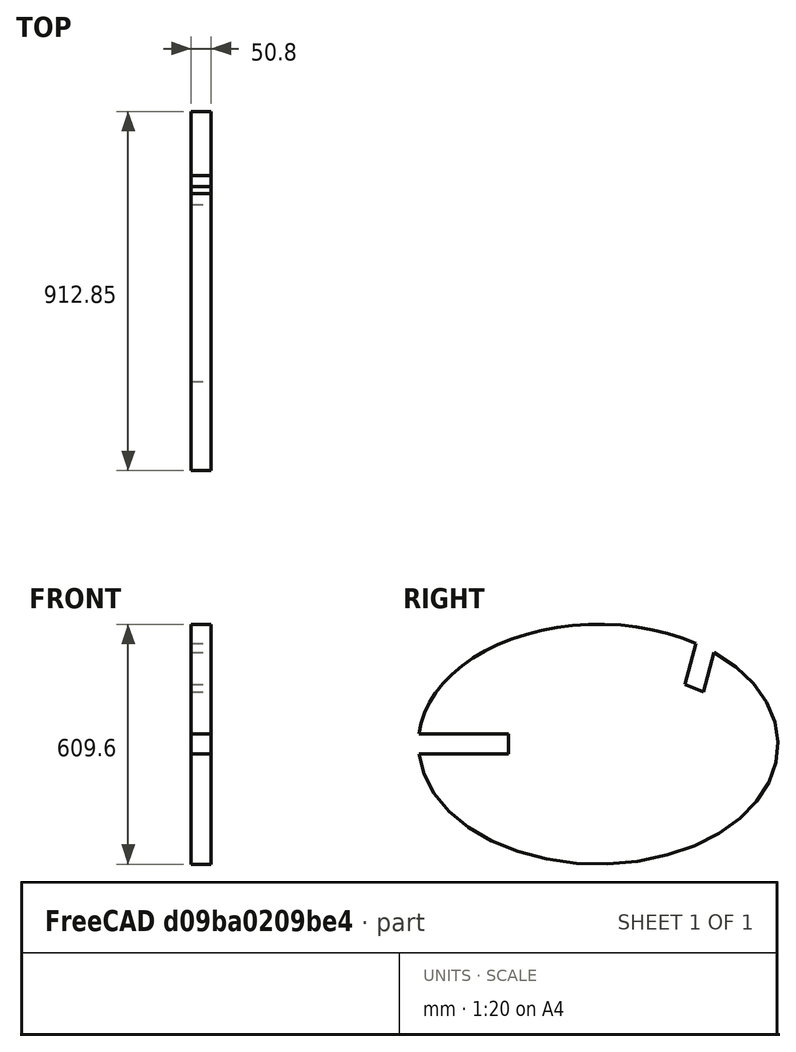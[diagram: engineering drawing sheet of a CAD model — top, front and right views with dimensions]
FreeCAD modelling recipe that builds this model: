
FCSTD DOCUMENT  (FreeCAD 0.21R33771 (Git))
Label: eclipse-2-side
License: All rights reserved
LicenseURL: http://en.wikipedia.org/wiki/All_rights_reserved
objects: Sketcher::SketchObject×1, PartDesign::Pad×1, PartDesign::Body×1, Spreadsheet::Sheet×1
note: 4 computed .brp shape members not serialized (recipe doc carries the construction recipe); baked Part::Feature solids carry a one-line shape summary decoded from their .brp

FEATURE [Sketcher::SketchObject] Sketch
  FullyConstrained = false
  MapMode = 5
  Placement = pos=(0,0,0) rot=(0.57735,0.57735,0.57735;2.0944rad)
  Support = -> [YZ_Plane]
  expr: Constraints[11] = <<dims>>.thickness
  expr: Constraints[18] = <<dims>>.thickness
  expr: Constraints[5] = <<dims>>.eclipse_height
  expr: Constraints[6] = <<dims>>.eclipse_length
  sketch-geometry (12):
    g0: ArcOfEllipse CenterX=0 CenterY=0 CenterZ=0 NormalX=0 NormalY=0 NormalZ=1 MajorRadius=457.2 MinorRadius=304.8 AngleXU=3.14063 StartAngle=0.082882 EndAngle=4.01486
    g1: LineSegment StartX=-457.2 StartY=0.438159 StartZ=0 EndX=457.2 EndY=-0.438159 EndZ=0
    g2: LineSegment StartX=-0.292106 StartY=-304.8 StartZ=0 EndX=0.292106 EndY=304.8 EndZ=0
    g3: GeomPoint X=-340.777 Y=0.326584 Z=0
    g4: GeomPoint X=340.777 Y=-0.326584 Z=0
    g5: LineSegment StartX=-455.564 StartY=26.0031 StartZ=0 EndX=-228.6 EndY=26.0031 EndZ=0
    g6: LineSegment StartX=-455.655 StartY=-24.7969 StartZ=0 EndX=-228.6 EndY=-24.7969 EndZ=0
    g7: LineSegment StartX=-228.6 StartY=-24.7969 StartZ=0 EndX=-228.6 EndY=26.0031 EndZ=0
    g8: LineSegment StartX=293.896 StartY=233.326 StartZ=0 EndX=266.795 EndY=132.569 EndZ=0
    g9: LineSegment StartX=247.974 StartY=255.942 StartZ=0 EndX=220.026 EndY=152.4 EndZ=0
    g10: LineSegment StartX=266.795 StartY=132.569 StartZ=0 EndX=220.026 EndY=152.4 EndZ=0
    g11: ArcOfEllipse CenterX=0 CenterY=0 CenterZ=0 NormalX=0 NormalY=0 NormalZ=1 MajorRadius=457.2 MinorRadius=304.8 AngleXU=3.14063 StartAngle=4.13977 EndAngle=6.19921
  constraints (20):
    c: InternalAlignment(g1-g4 -> g0) x4
    c: Coincident(g0,g-1)
    c: DistanceY(g2,g2) = 609.6
    c: DistanceX(g1,g1) = 914.4
    c: Horizontal(g5)
    c: Coincident(g7,g6)
    c: Coincident(g7,g5)
    c: Vertical(g7)
    c: DistanceY(g7,g7) = 50.8
    c: Horizontal(g6)
    c: Coincident(g6,g0)
    c: Coincident(g5,g11)
    c: Angle(g8,g1) = 1.8326
    c: Coincident(g9,g10)
    c: Coincident(g8,g10)
    c: Distance(g9,g8) = 50.8
    c: Equal(g0,g11)
    c: Coincident(g0,g8)
    c: Coincident(g11,g9)
    c: Coincident(g0,g11)
FEATURE [PartDesign::Pad] Pad
  Direction = (1,-2e-16,3e-16)
  Length = 50.8
  Length2 = 10
  Placement = pos=(0,0,0) rot=(1,1,1;2.0944rad)
  Profile = -> Sketch
  ReferenceAxis = -> Sketch [N_Axis]
  Type = 0
  expr: Length = <<dims>>.thickness
FEATURE [PartDesign::Body] Body
  Group = -> [Sketch,Pad]
  Origin = -> Origin
  Tip = -> Pad
FEATURE [Spreadsheet::Sheet] Spreadsheet  label="dims"
  cells = B2='eclipse_length; C2(eclipse_length)==36 in; B3='eclipse_height; C3(eclipse_height)==24 in; B4='thickness; C4(thickness)==2 in; B5='slot_from_end; C5(slot_from_end)==6 in; B6='seat_length; C6(seat_length)==48 in
